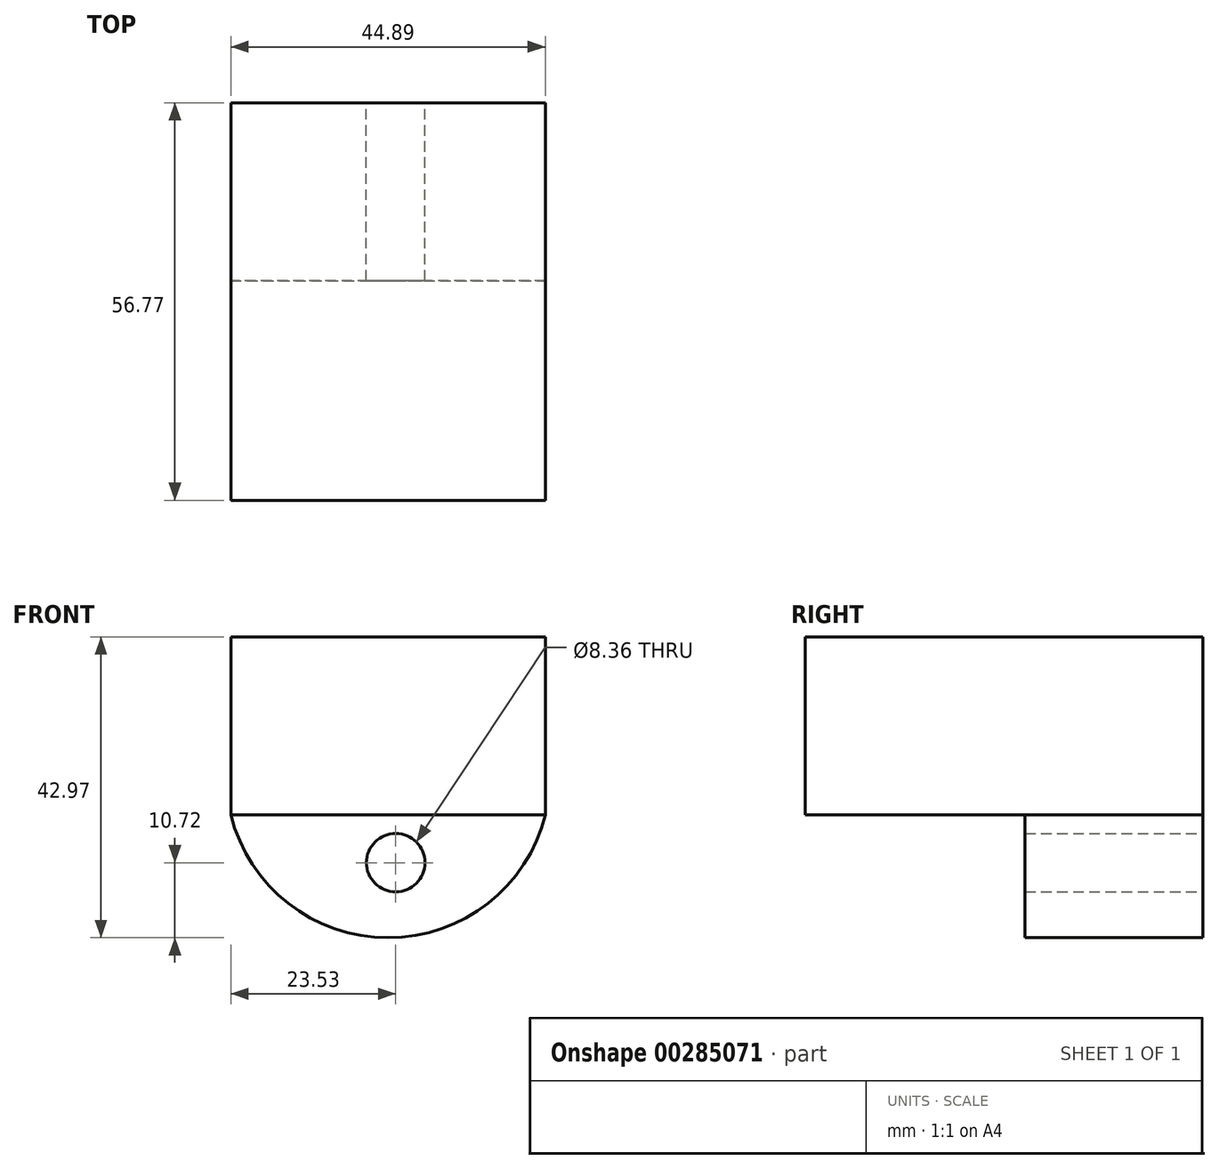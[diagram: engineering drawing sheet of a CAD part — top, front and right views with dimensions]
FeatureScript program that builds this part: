
annotation { "Feature Type Name" : "Feature", "Feature Type Description" : "" }
export const myFeature = defineFeature(function(context is Context, id is Id, definition is map)
    precondition{}
    {
        {
            var Q0;
            Q0=qCreatedBy(makeId("Top.planeOp"),FACE);
            var sketch = newSketch(context, id + "F0", { "sketchPlane" : qUnion([Q0])});
            skLineSegment(sketch, "E0.bottom", {"start": v(-58.42, 27.63) * mm, "end": v(-13.53, 27.63) * mm});
            skLineSegment(sketch, "E0.top", {"start": v(-58.42, -3.74) * mm, "end": v(-13.53, -3.74) * mm});
            skLineSegment(sketch, "E0.left", {"start": v(-58.42, 27.63) * mm, "end": v(-58.42, -3.74) * mm});
            skLineSegment(sketch, "E0.right", {"start": v(-13.53, 27.63) * mm, "end": v(-13.53, -3.74) * mm});
            skArc(sketch, "E1", {"start": v(-13.53, 27.63) * mm, "mid": v(-35.98, 45.86) * mm, "end": v(-58.42, 27.63) * mm});
            skSolve(sketch);
        }
        {
            var Q0;
            Q0=makeQuery(id+"F0.imprint","IMPRINT",FACE,{"disambiguationData":[TD([[makeQuery(id+"F0.imprint","IMPRINT",EDGE,{"derivedFrom":sQuery(id+"F0.wireOp",EDGE,"E0.bottom")}),-1.0]])]});
            extrude(context, id + "F1", {"entities" : qUnion([Q0]), "depth" : 25.4 * mm});
        }
        {
            var Q0;
            Q0=makeQuery(id+"F1.opExtrude","SWEPT_FACE",FACE,{"disambiguationData":[OSD([sQuery(id+"F0.wireOp",EDGE,"E0.bottom")])]});
            var sketch = newSketch(context, id + "F2", { "sketchPlane" : qUnion([Q0])});
            skArc(sketch, "E2", {"start": v(13.53, 0) * mm, "mid": v(35.98, -17.57) * mm, "end": v(58.42, 0) * mm});
            skSolve(sketch);
        }
        {
            var Q0;
            Q0 = qSketchRegion(id + "F2", true);
            var Q1;
            Q1=makeQuery(id+"F2.imprint","IMPRINT",FACE,{"disambiguationData":[TD([[makeQuery(id+"F2.imprint","IMPRINT",EDGE,{"derivedFrom":sQuery(id+"F2.wireOp",EDGE,"E2")}),1.0]])]});
            var Q2;
            {var subQ1=sQuery(id+"F0.wireOp",EDGE,"E0.bottom");Q2=makeQuery(id+"F2.imprint","IMPRINT",FACE,{"disambiguationData":[TD([[makeQuery(id+"F2.imprint","IMPRINT",EDGE,{"derivedFrom":makeQuery(id+"F1.opExtrude","CAP_EDGE",EDGE,{"disambiguationData":[OSD([subQ1])],"isStart":true})}),-1.0]])]});}
            extrude(context, id + "F3", {"entities" : qUnion([Q0, Q1, Q2]), "operationType" : NewBodyOperationType.ADD, "depth" : 25.4 * mm});
        }
        {
            var Q0;
            Q0=makeQuery(id+"F3.opExtrude","CAP_FACE",FACE,{"disambiguationData":[OSD([sQuery(id+"F0.wireOp",EDGE,"E0.bottom"),sQuery(id+"F0.wireOp",EDGE,"E0.left"),sQuery(id+"F0.wireOp",EDGE,"E0.right"),sQuery(id+"F0.wireOp",EDGE,"E1"),sQuery(id+"F2.wireOp",EDGE,"E2")])],"isStart":false});
            var sketch = newSketch(context, id + "F4", { "sketchPlane" : qUnion([Q0])});
            skCircle(sketch, "E3", {"center": v(34.9, -6.85) * mm, "radius": 4.18 * mm});
            skSolve(sketch);
        }
        {
            var Q0;
            Q0=makeQuery(id+"F4.imprint","IMPRINT",FACE,{"disambiguationData":[TD([[makeQuery(id+"F4.imprint","IMPRINT",EDGE,{"derivedFrom":sQuery(id+"F4.wireOp",EDGE,"E3")}),1.0]])]});
            extrude(context, id + "F5", {"entities" : qUnion([Q0]), "operationType" : NewBodyOperationType.REMOVE, "oppositeDirection" : true, "depth" : 25.4 * mm});
        }
    });
